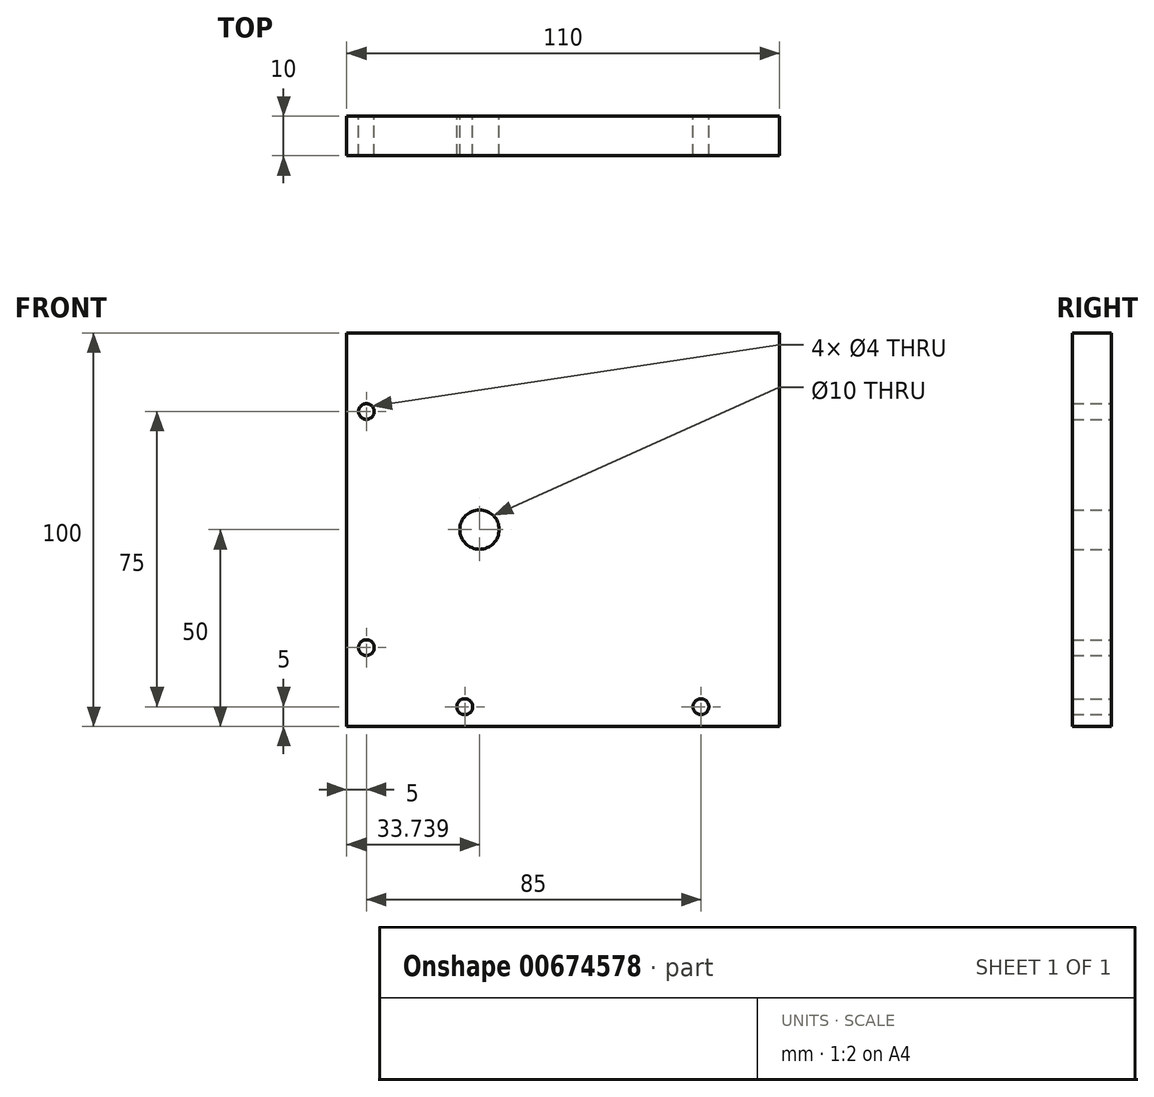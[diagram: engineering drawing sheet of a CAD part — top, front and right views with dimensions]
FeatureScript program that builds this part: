
annotation { "Feature Type Name" : "Feature", "Feature Type Description" : "" }
export const myFeature = defineFeature(function(context is Context, id is Id, definition is map)
    precondition{}
    {
        {
            var Q0;
            Q0=qCreatedBy(makeId("Front.planeOp"),FACE);
            var sketch = newSketch(context, id + "F0", { "sketchPlane" : qUnion([Q0])});
            skLineSegment(sketch, "E0.bottom", {"start": v(55, 50) * mm, "end": v(-55, 50) * mm});
            skLineSegment(sketch, "E0.top", {"start": v(55, -50) * mm, "end": v(-55, -50) * mm});
            skLineSegment(sketch, "E0.left", {"start": v(55, 50) * mm, "end": v(55, -50) * mm});
            skLineSegment(sketch, "E0.right", {"start": v(-55, 50) * mm, "end": v(-55, -50) * mm});
            skCircle(sketch, "E1", {"center": v(-25, -45) * mm, "radius": 2 * mm});
            skCircle(sketch, "E2", {"center": v(35, -45) * mm, "radius": 2 * mm});
            skCircle(sketch, "E3", {"center": v(-50, 30) * mm, "radius": 2 * mm});
            skCircle(sketch, "E4", {"center": v(-50, -30) * mm, "radius": 2 * mm});
            skCircle(sketch, "E5", {"center": v(-21.26, 0) * mm, "radius": 5 * mm});
            skSolve(sketch);
        }
        {
            var Q0;
            Q0=makeQuery(id+"F0.imprint","IMPRINT",FACE,{"disambiguationData":[TD([[makeQuery(id+"F0.imprint","IMPRINT",EDGE,{"derivedFrom":sQuery(id+"F0.wireOp",EDGE,"E0.bottom")}),1.0]])]});
            extrude(context, id + "F1", {"entities" : qUnion([Q0]), "depth" : 10 * mm, "offsetDistance" : 25 * mm});
        }
    });
